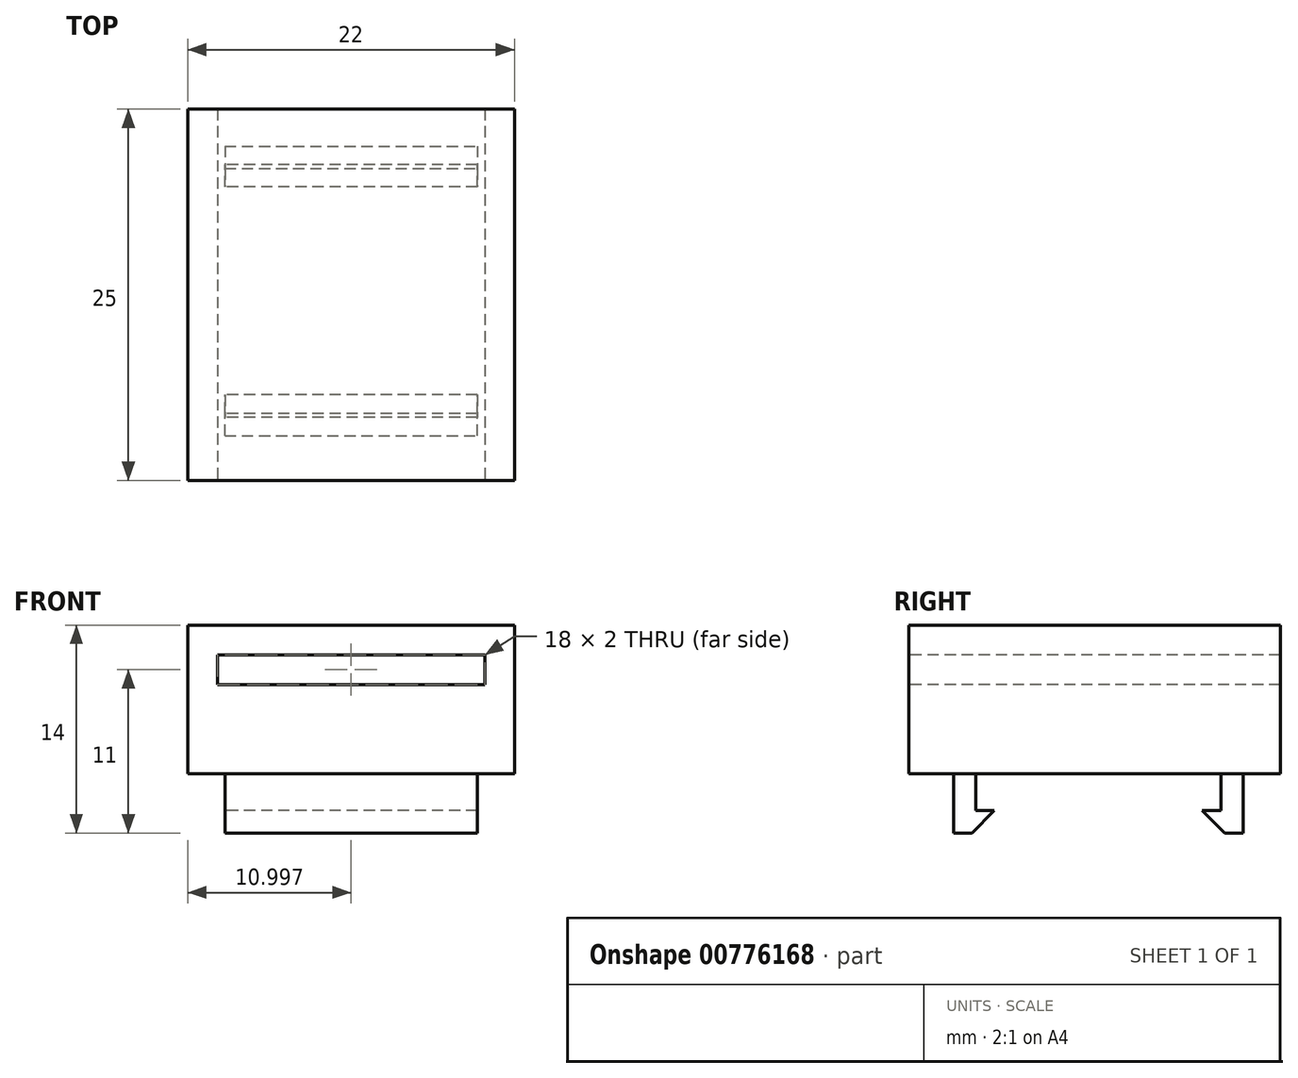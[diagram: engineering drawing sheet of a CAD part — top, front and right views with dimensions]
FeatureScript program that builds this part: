
annotation { "Feature Type Name" : "Feature", "Feature Type Description" : "" }
export const myFeature = defineFeature(function(context is Context, id is Id, definition is map)
    precondition{}
    {
        {
            var Q0;
            Q0=qCreatedBy(makeId("Top.planeOp"),FACE);
            var sketch = newSketch(context, id + "F0", { "sketchPlane" : qUnion([Q0])});
            skLineSegment(sketch, "E0.bottom", {"start": v(-8.11, -4.6) * mm, "end": v(13.89, -4.6) * mm});
            skLineSegment(sketch, "E0.top", {"start": v(-8.11, 20.4) * mm, "end": v(13.89, 20.4) * mm});
            skLineSegment(sketch, "E0.left", {"start": v(-8.11, -4.6) * mm, "end": v(-8.11, 20.4) * mm});
            skLineSegment(sketch, "E0.right", {"start": v(13.89, -4.6) * mm, "end": v(13.89, 20.4) * mm});
            skSolve(sketch);
        }
        {
            var Q0;
            Q0=makeQuery(id+"F0.imprint","IMPRINT",FACE,{"disambiguationData":[TD([[makeQuery(id+"F0.imprint","IMPRINT",EDGE,{"derivedFrom":sQuery(id+"F0.wireOp",EDGE,"E0.bottom")}),1.0]])]});
            extrude(context, id + "F1", {"entities" : qUnion([Q0]), "depth" : 10 * mm, "offsetDistance" : 25 * mm});
        }
        {
            var Q0;
            Q0=makeQuery(id+"F1.opExtrude","SWEPT_FACE",FACE,{"disambiguationData":[OSD([sQuery(id+"F0.wireOp",EDGE,"E0.bottom")])]});
            var sketch = newSketch(context, id + "F2", { "sketchPlane" : qUnion([Q0])});
            skLineSegment(sketch, "E1.bottom", {"start": v(-6.11, 8) * mm, "end": v(11.89, 8) * mm});
            skLineSegment(sketch, "E1.top", {"start": v(-6.11, 6) * mm, "end": v(11.89, 6) * mm});
            skLineSegment(sketch, "E1.left", {"start": v(-6.11, 8) * mm, "end": v(-6.11, 6) * mm});
            skLineSegment(sketch, "E1.right", {"start": v(11.89, 8) * mm, "end": v(11.89, 6) * mm});
            skSolve(sketch);
        }
        {
            var Q0;
            Q0=makeQuery(id+"F2.imprint","IMPRINT",FACE,{"disambiguationData":[TD([[makeQuery(id+"F2.imprint","IMPRINT",EDGE,{"derivedFrom":sQuery(id+"F2.wireOp",EDGE,"E1.bottom")}),-1.0]])]});
            var Q1;
            Q1=makeQuery(id+"F1.opExtrude","SWEPT_FACE",FACE,{"disambiguationData":[OSD([sQuery(id+"F0.wireOp",EDGE,"E0.top")])]});
            extrude(context, id + "F3", {"entities" : qUnion([Q0]), "operationType" : NewBodyOperationType.REMOVE, "endBound" : BoundingType.UP_TO_SURFACE, "oppositeDirection" : true, "depth" : 25 * mm, "endBoundEntityFace" : qUnion([Q1]), "offsetDistance" : 25 * mm});
        }
        {
            var Q0;
            Q0=makeQuery(id+"F1.opExtrude","CAP_FACE",FACE,{"disambiguationData":[OSD([sQuery(id+"F0.wireOp",EDGE,"E0.bottom"),sQuery(id+"F0.wireOp",EDGE,"E0.top"),sQuery(id+"F0.wireOp",EDGE,"E0.left"),sQuery(id+"F0.wireOp",EDGE,"E0.right")])],"isStart":true});
            var sketch = newSketch(context, id + "F4", { "sketchPlane" : qUnion([Q0])});
            skLineSegment(sketch, "E2.bottom", {"start": v(-5.61, 1.6) * mm, "end": v(11.39, 1.6) * mm});
            skLineSegment(sketch, "E2.top", {"start": v(-5.61, 0.1) * mm, "end": v(11.39, 0.1) * mm});
            skLineSegment(sketch, "E2.left", {"start": v(-5.61, 1.6) * mm, "end": v(-5.61, 0.1) * mm});
            skLineSegment(sketch, "E2.right", {"start": v(11.39, 1.6) * mm, "end": v(11.39, 0.1) * mm});
            skLineSegment(sketch, "E3", {"start": v(2.89, 1.6) * mm, "end": v(2.89, -6.34) * mm, "construction": true});
            skLineSegment(sketch, "E4", {"start": v(2.89, 4.6) * mm, "end": v(2.89, -10.96) * mm, "construction": true});
            skSolve(sketch);
        }
        {
            var Q0;
            Q0=makeQuery(id+"F4.imprint","IMPRINT",FACE,{"disambiguationData":[TD([[makeQuery(id+"F4.imprint","IMPRINT",EDGE,{"derivedFrom":sQuery(id+"F4.wireOp",EDGE,"E2.bottom")}),-1.0]])]});
            extrude(context, id + "F5", {"entities" : qUnion([Q0]), "depth" : 4 * mm, "offsetDistance" : 25 * mm});
        }
        {
            var Q0;
            Q0=makeQuery(id+"F5.opExtrude","SWEPT_FACE",FACE,{"disambiguationData":[OSD([sQuery(id+"F4.wireOp",EDGE,"E2.left")])]});
            var sketch = newSketch(context, id + "F6", { "sketchPlane" : qUnion([Q0])});
            skPoint(sketch, "E5.orphan", {"position": v(0.1, -5.5) * mm});
            skLineSegment(sketch, "E6", {"start": v(0.1, -2.5) * mm, "end": v(-1.14, -2.5) * mm});
            skLineSegment(sketch, "E7", {"start": v(-1.14, -2.5) * mm, "end": v(0.36, -4) * mm});
            skLineSegment(sketch, "E8", {"start": v(0.1, -2.5) * mm, "end": v(0.1, -3.75) * mm});
            skSolve(sketch);
        }
        {
            var Q0;
            Q0 = qSketchRegion(id + "F6", true);
            var Q1;
            Q1=makeQuery(id+"F5.opExtrude","SWEPT_FACE",FACE,{"disambiguationData":[OSD([sQuery(id+"F4.wireOp",EDGE,"E2.right")])]});
            extrude(context, id + "F7", {"entities" : qUnion([Q0]), "operationType" : NewBodyOperationType.ADD, "endBound" : BoundingType.UP_TO_SURFACE, "oppositeDirection" : true, "depth" : 25 * mm, "endBoundEntityFace" : qUnion([Q1]), "offsetDistance" : 25 * mm});
        }
        {
            var Q0;
            {var subQ0=sQuery(id+"F6.wireOp",EDGE,"E7");var subQ1=sQuery(id+"F4.wireOp",EDGE,"E2.left");var subQ2=makeQuery(id+"F5.opExtrude","CAP_EDGE",EDGE,{"disambiguationData":[OSD([subQ1])],"isStart":false});var subQ3=makeQuery(id+"F6.imprint","INTERSECT",VERTEX,{"derivedFrom":[subQ2,subQ0]});Q0=makeQuery(id+"F6.imprint","IMPRINT",FACE,{"disambiguationData":[TD([[makeQuery(id+"F6.imprint","IMPRINT",EDGE,{"disambiguationData":[TD([[subQ3,-1.0]])],"derivedFrom":subQ2}),-1.0]])]});}
            var Q1;
            {var subQ0=sQuery(id+"F4.wireOp",EDGE,"E2.right");Q1=makeQuery(id+"F7.boolean.opBoolean","MERGE",FACE,{"derivedFrom":[makeQuery(id+"F5.opExtrude","SWEPT_FACE",FACE,{"disambiguationData":[OSD([subQ0])]}),makeQuery(id+"F7.opExtrude","CAP_FACE",FACE,{"disambiguationData":[OSD([subQ0])],"isStart":false})]});}
            extrude(context, id + "F8", {"entities" : qUnion([Q0]), "operationType" : NewBodyOperationType.REMOVE, "endBound" : BoundingType.UP_TO_SURFACE, "oppositeDirection" : true, "depth" : 25 * mm, "endBoundEntityFace" : qUnion([Q1]), "offsetDistance" : 25 * mm});
        }
        {
            var Q0;
            Q0=makeQuery(id+"F5.opExtrude","SWEPT_BODY",BODY,{"disambiguationData":[OSD([sQuery(id+"F4.wireOp",EDGE,"E2.bottom"),sQuery(id+"F4.wireOp",EDGE,"E2.top"),sQuery(id+"F4.wireOp",EDGE,"E2.left"),sQuery(id+"F4.wireOp",EDGE,"E2.right")])]});
            var Q1;
            Q1=makeQuery(id+"F5.opExtrude","SWEPT_FACE",FACE,{"disambiguationData":[OSD([sQuery(id+"F4.wireOp",EDGE,"E2.top")])]});
            mirror(context, id + "F9", {"entities" : qUnion([Q0]), "mirrorPlane" : qUnion([Q1])});
        }
        {
            var Q0;
            Q0=makeQuery(id+"F9.opPattern","COPY",BODY,{"derivedFrom":makeQuery(id+"F5.opExtrude","SWEPT_BODY",BODY,{"disambiguationData":[OSD([sQuery(id+"F4.wireOp",EDGE,"E2.bottom"),sQuery(id+"F4.wireOp",EDGE,"E2.top"),sQuery(id+"F4.wireOp",EDGE,"E2.left"),sQuery(id+"F4.wireOp",EDGE,"E2.right")])]}),"instanceName":"1"});
            transform(context, id + "F10", {"entities" : qUnion([Q0]), "transformType" : TransformType.TRANSLATION_3D, "dx" : 0 * mm, "dy" : 16.5 * mm, "dz" : 0 * mm, "makeCopy" : false});
        }
    });
